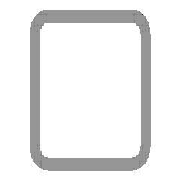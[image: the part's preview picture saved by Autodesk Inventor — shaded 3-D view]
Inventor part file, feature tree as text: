
AUTODESK INVENTOR PART (.ipt)
format: ipt  version: 2016 (Build 200138000, 138)  size: 129,024 bytes
history: native  units: mm (DEFAULTED — no unit token found)
features: other x4, sketch x3, plane x1
ambient origin geometry x8: Origin, YZ Plane, XZ Plane, XY Plane, X Axis, Y Axis, Z Axis, Center Point
bodies: Solid1 (feature_tree), Body (feature_tree)
feature tree (8):
  parser-record x1  (decoder bookkeeping rows leaked as tree rows — omitted from the tree; the rows remain in map.json)
  other  "Driven Length"
  other  "Start plane"
  other  "End plane"
  sketch  "Sketch"  dims[d7=4.0mm d9=60.0mm d11=60.0mm d12=2.0mm d13=-0.0mm d14=642.017003mm d15=30.0mm d16=30.0mm d17=90.0deg d18=642.017003mm]
  sketch  "Sketch3"  dims[d3=642.017003mm]
  plane  "Work Plane3"
  sketch  "Sketch4"  dims[d4=0.0mm]
